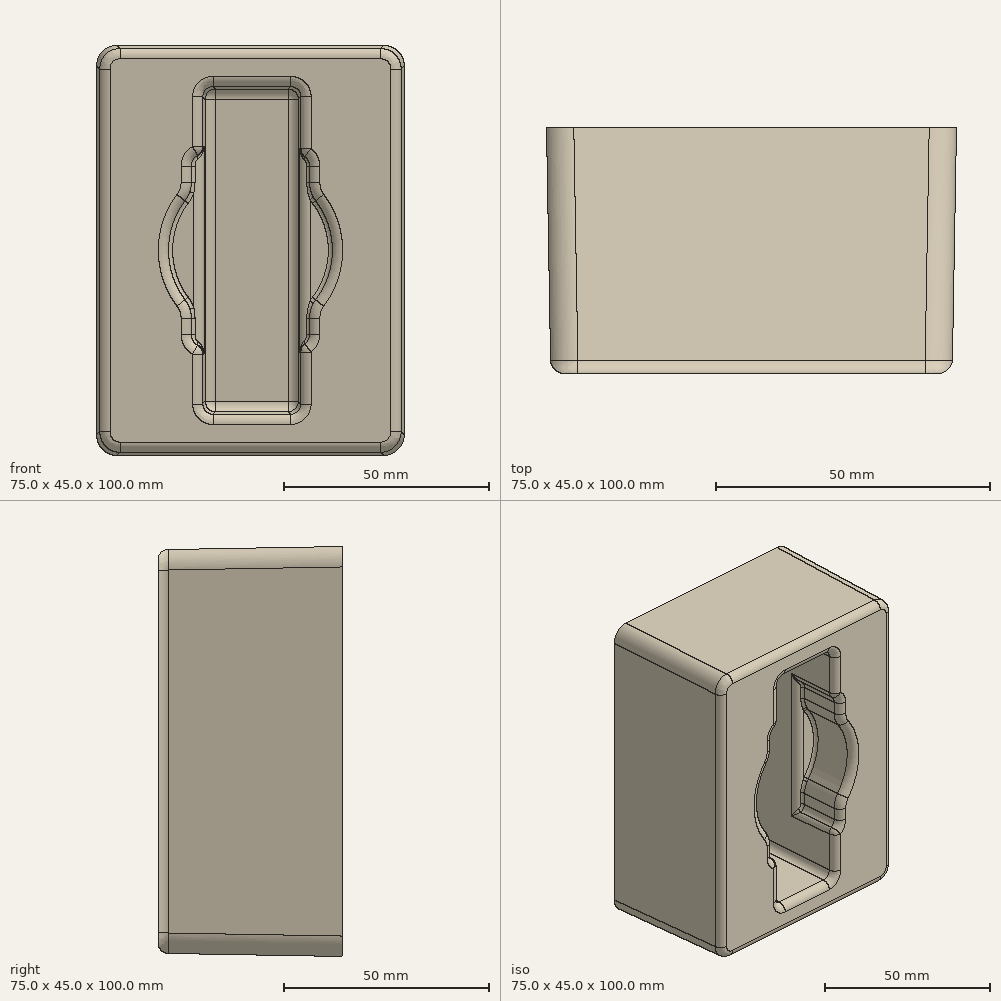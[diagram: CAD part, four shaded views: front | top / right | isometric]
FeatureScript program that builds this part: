
annotation { "Feature Type Name" : "Feature", "Feature Type Description" : "" }
export const myFeature = defineFeature(function(context is Context, id is Id, definition is map)
    precondition{}
    {
        {
            var Q0;
            Q0=qCreatedBy(makeId("Front.planeOp"),FACE);
            var sketch = newSketch(context, id + "F0", { "sketchPlane" : qUnion([Q0])});
            skLineSegment(sketch, "E0.bottom", {"start": v(0, 0) * mm, "end": v(75, 0) * mm});
            skLineSegment(sketch, "E0.top", {"start": v(0, 100) * mm, "end": v(75, 100) * mm});
            skLineSegment(sketch, "E0.left", {"start": v(0, 0) * mm, "end": v(0, 100) * mm});
            skLineSegment(sketch, "E0.right", {"start": v(75, 0) * mm, "end": v(75, 100) * mm});
            skSolve(sketch);
        }
        {
            var Q0;
            Q0=makeQuery(id+"F0.imprint","IMPRINT",FACE,{"disambiguationData":[TD([[makeQuery(id+"F0.imprint","IMPRINT",EDGE,{"derivedFrom":sQuery(id+"F0.wireOp",EDGE,"E0.bottom")}),1.0]])]});
            extrude(context, id + "F1", {"entities" : qUnion([Q0]), "depth" : 45 * mm, "hasDraft" : true, "draftAngle" : 1 * degree, "draftPullDirection" : true});
        }
        {
            var Q0;
            Q0=makeQuery(id+"F1.opExtrude","CAP_FACE",FACE,{"disambiguationData":[OSD([sQuery(id+"F0.wireOp",EDGE,"E0.bottom"),sQuery(id+"F0.wireOp",EDGE,"E0.top"),sQuery(id+"F0.wireOp",EDGE,"E0.left"),sQuery(id+"F0.wireOp",EDGE,"E0.right")])],"isStart":false});
            var sketch = newSketch(context, id + "F2", { "sketchPlane" : qUnion([Q0])});
            skArc(sketch, "E1", {"start": v(21.57, 62.1) * mm, "mid": v(17.5, 50) * mm, "end": v(21.57, 37.9) * mm});
            skLineSegment(sketch, "E2.bottom", {"start": v(48.9, 26.5) * mm, "end": v(26.1, 26.5) * mm});
            skLineSegment(sketch, "E2.top", {"start": v(48.9, 73.5) * mm, "end": v(26.1, 73.5) * mm});
            skLineSegment(sketch, "E2.left", {"start": v(51.9, 29.5) * mm, "end": v(51.9, 33.37) * mm});
            skLineSegment(sketch, "E2.right", {"start": v(23.1, 29.5) * mm, "end": v(23.1, 33.37) * mm});
            skLineSegment(sketch, "E3.trimOffspring", {"start": v(23.1, 66.63) * mm, "end": v(23.1, 70.5) * mm});
            skArc(sketch, "E4.trimOffspring", {"start": v(53.43, 37.9) * mm, "mid": v(57.5, 50) * mm, "end": v(53.43, 62.1) * mm});
            skLineSegment(sketch, "E5.trimOffspring", {"start": v(51.9, 66.63) * mm, "end": v(51.9, 70.5) * mm});
            skPoint(sketch, "E6.visualSharp", {"position": v(23.1, 63.88) * mm});
            skArc(sketch, "E6.filletArc", {"start": v(21.57, 62.1) * mm, "mid": v(22.7, 64.24) * mm, "end": v(23.1, 66.63) * mm});
            skPoint(sketch, "E7.visualSharp", {"position": v(51.9, 63.88) * mm});
            skArc(sketch, "E7.filletArc", {"start": v(51.9, 66.63) * mm, "mid": v(52.3, 64.24) * mm, "end": v(53.43, 62.1) * mm});
            skPoint(sketch, "E8.visualSharp", {"position": v(23.1, 36.12) * mm});
            skArc(sketch, "E8.filletArc", {"start": v(23.1, 33.37) * mm, "mid": v(22.7, 35.76) * mm, "end": v(21.57, 37.9) * mm});
            skPoint(sketch, "E9.visualSharp", {"position": v(51.9, 36.12) * mm});
            skArc(sketch, "E9.filletArc", {"start": v(53.43, 37.9) * mm, "mid": v(52.3, 35.76) * mm, "end": v(51.9, 33.37) * mm});
            skPoint(sketch, "E10.visualSharp", {"position": v(23.1, 73.5) * mm});
            skArc(sketch, "E10.filletArc", {"start": v(26.1, 73.5) * mm, "mid": v(23.97, 72.62) * mm, "end": v(23.1, 70.5) * mm});
            skPoint(sketch, "E11.visualSharp", {"position": v(51.9, 73.5) * mm});
            skArc(sketch, "E11.filletArc", {"start": v(51.9, 70.5) * mm, "mid": v(51.03, 72.62) * mm, "end": v(48.9, 73.5) * mm});
            skPoint(sketch, "E12.visualSharp", {"position": v(23.1, 26.5) * mm});
            skArc(sketch, "E12.filletArc", {"start": v(23.1, 29.5) * mm, "mid": v(23.97, 27.38) * mm, "end": v(26.1, 26.5) * mm});
            skPoint(sketch, "E13.visualSharp", {"position": v(51.9, 26.5) * mm});
            skArc(sketch, "E13.filletArc", {"start": v(48.9, 26.5) * mm, "mid": v(51.03, 27.38) * mm, "end": v(51.9, 29.5) * mm});
            skSolve(sketch);
        }
        {
            var Q0;
            Q0=makeQuery(id+"F2.imprint","IMPRINT",FACE,{"disambiguationData":[TD([[makeQuery(id+"F2.imprint","IMPRINT",EDGE,{"derivedFrom":sQuery(id+"F2.wireOp",EDGE,"E1")}),-1.0]])]});
            var sketch = newSketch(context, id + "F3", { "sketchPlane" : qUnion([Q0])});
            skLineSegment(sketch, "E14.bottom", {"start": v(49.85, 10) * mm, "end": v(25.85, 10) * mm});
            skLineSegment(sketch, "E14.top", {"start": v(49.85, 90) * mm, "end": v(25.85, 90) * mm});
            skLineSegment(sketch, "E14.left", {"start": v(49.85, 10) * mm, "end": v(49.85, 90) * mm});
            skLineSegment(sketch, "E14.right", {"start": v(25.85, 10) * mm, "end": v(25.85, 90) * mm});
            skPoint(sketch, "E14.middle", {"position": v(37.85, 50) * mm});
            skSolve(sketch);
        }
        {
            var Q0;
            Q0 = qSketchRegion(id + "F3", true);
            extrude(context, id + "F4", {"entities" : qUnion([Q0]), "operationType" : NewBodyOperationType.REMOVE, "oppositeDirection" : true, "depth" : 40 * mm, "hasDraft" : true, "draftAngle" : 1 * degree, "draftPullDirection" : true});
        }
        {
            var Q0;
            Q0 = qSketchRegion(id + "F2", true);
            extrude(context, id + "F5", {"entities" : qUnion([Q0]), "operationType" : NewBodyOperationType.REMOVE, "oppositeDirection" : true, "depth" : 16 * mm});
        }
        {
            var Q0;
            Q0=makeQuery(id+"F1.opExtrude","CAP_FACE",FACE,{"disambiguationData":[OSD([sQuery(id+"F0.wireOp",EDGE,"E0.bottom"),sQuery(id+"F0.wireOp",EDGE,"E0.top"),sQuery(id+"F0.wireOp",EDGE,"E0.left"),sQuery(id+"F0.wireOp",EDGE,"E0.right")])],"isStart":false});
            var Q1;
            Q1=makeQuery(id+"F4.boolean.opBoolean","COPY",EDGE,{"derivedFrom":makeQuery(id+"F4.opExtrude","SWEPT_EDGE",EDGE,{"disambiguationData":[OSD([sQuery(id+"F3.wireOp",EDGE,"E14.top"),sQuery(id+"F3.wireOp",EDGE,"E14.right")])]})});
            var Q2;
            Q2=makeQuery(id+"F4.boolean.opBoolean","COPY",EDGE,{"derivedFrom":makeQuery(id+"F4.opExtrude","SWEPT_EDGE",EDGE,{"disambiguationData":[OSD([sQuery(id+"F3.wireOp",EDGE,"E14.top"),sQuery(id+"F3.wireOp",EDGE,"E14.left")])]})});
            var Q3;
            Q3=makeQuery(id+"F4.boolean.opBoolean","COPY",FACE,{"derivedFrom":makeQuery(id+"F4.opExtrude","SWEPT_FACE",FACE,{"disambiguationData":[OSD([sQuery(id+"F3.wireOp",EDGE,"E14.bottom")])]})});
            var Q4;
            Q4=makeQuery(id+"F4.boolean.opBoolean","COPY",FACE,{"derivedFrom":makeQuery(id+"F4.opExtrude","CAP_FACE",FACE,{"disambiguationData":[OSD([sQuery(id+"F3.wireOp",EDGE,"E14.bottom"),sQuery(id+"F3.wireOp",EDGE,"E14.top"),sQuery(id+"F3.wireOp",EDGE,"E14.left"),sQuery(id+"F3.wireOp",EDGE,"E14.right")])],"isStart":false})});
            var Q5;
            Q5=makeQuery(id+"F5.boolean.opBoolean","INTERSECT",EDGE,{"derivedFrom":[makeQuery(id+"F4.boolean.opBoolean","COPY",FACE,{"derivedFrom":makeQuery(id+"F4.opExtrude","SWEPT_FACE",FACE,{"disambiguationData":[OSD([sQuery(id+"F3.wireOp",EDGE,"E14.right")])]})}),makeQuery(id+"F5.opExtrude","SWEPT_FACE",FACE,{"disambiguationData":[OSD([sQuery(id+"F2.wireOp",EDGE,"E10.filletArc")])]})]});
            var Q6;
            Q6=makeQuery(id+"F5.boolean.opBoolean","INTERSECT",EDGE,{"derivedFrom":[makeQuery(id+"F4.boolean.opBoolean","COPY",FACE,{"derivedFrom":makeQuery(id+"F4.opExtrude","SWEPT_FACE",FACE,{"disambiguationData":[OSD([sQuery(id+"F3.wireOp",EDGE,"E14.right")])]})}),makeQuery(id+"F5.opExtrude","CAP_FACE",FACE,{"disambiguationData":[OSD([sQuery(id+"F2.wireOp",EDGE,"E1"),sQuery(id+"F2.wireOp",EDGE,"E2.bottom"),sQuery(id+"F2.wireOp",EDGE,"E2.top"),sQuery(id+"F2.wireOp",EDGE,"E2.left"),sQuery(id+"F2.wireOp",EDGE,"E2.right"),sQuery(id+"F2.wireOp",EDGE,"E3.trimOffspring"),sQuery(id+"F2.wireOp",EDGE,"E4.trimOffspring"),sQuery(id+"F2.wireOp",EDGE,"E5.trimOffspring"),sQuery(id+"F2.wireOp",EDGE,"E6.filletArc"),sQuery(id+"F2.wireOp",EDGE,"E7.filletArc"),sQuery(id+"F2.wireOp",EDGE,"E8.filletArc"),sQuery(id+"F2.wireOp",EDGE,"E9.filletArc"),sQuery(id+"F2.wireOp",EDGE,"E10.filletArc"),sQuery(id+"F2.wireOp",EDGE,"E11.filletArc"),sQuery(id+"F2.wireOp",EDGE,"E12.filletArc"),sQuery(id+"F2.wireOp",EDGE,"E13.filletArc")])],"isStart":false})]});
            var Q7;
            Q7=makeQuery(id+"F5.boolean.opBoolean","INTERSECT",EDGE,{"derivedFrom":[makeQuery(id+"F4.boolean.opBoolean","COPY",FACE,{"derivedFrom":makeQuery(id+"F4.opExtrude","SWEPT_FACE",FACE,{"disambiguationData":[OSD([sQuery(id+"F3.wireOp",EDGE,"E14.right")])]})}),makeQuery(id+"F5.opExtrude","SWEPT_FACE",FACE,{"disambiguationData":[OSD([sQuery(id+"F2.wireOp",EDGE,"E12.filletArc")])]})]});
            var Q8;
            Q8=makeQuery(id+"F5.boolean.opBoolean","INTERSECT",EDGE,{"derivedFrom":[makeQuery(id+"F4.boolean.opBoolean","COPY",FACE,{"derivedFrom":makeQuery(id+"F4.opExtrude","SWEPT_FACE",FACE,{"disambiguationData":[OSD([sQuery(id+"F3.wireOp",EDGE,"E14.left")])]})}),makeQuery(id+"F5.opExtrude","SWEPT_FACE",FACE,{"disambiguationData":[OSD([sQuery(id+"F2.wireOp",EDGE,"E11.filletArc")])]})]});
            var Q9;
            Q9=makeQuery(id+"F5.boolean.opBoolean","INTERSECT",EDGE,{"derivedFrom":[makeQuery(id+"F4.boolean.opBoolean","COPY",FACE,{"derivedFrom":makeQuery(id+"F4.opExtrude","SWEPT_FACE",FACE,{"disambiguationData":[OSD([sQuery(id+"F3.wireOp",EDGE,"E14.left")])]})}),makeQuery(id+"F5.opExtrude","CAP_FACE",FACE,{"disambiguationData":[OSD([sQuery(id+"F2.wireOp",EDGE,"E1"),sQuery(id+"F2.wireOp",EDGE,"E2.bottom"),sQuery(id+"F2.wireOp",EDGE,"E2.top"),sQuery(id+"F2.wireOp",EDGE,"E2.left"),sQuery(id+"F2.wireOp",EDGE,"E2.right"),sQuery(id+"F2.wireOp",EDGE,"E3.trimOffspring"),sQuery(id+"F2.wireOp",EDGE,"E4.trimOffspring"),sQuery(id+"F2.wireOp",EDGE,"E5.trimOffspring"),sQuery(id+"F2.wireOp",EDGE,"E6.filletArc"),sQuery(id+"F2.wireOp",EDGE,"E7.filletArc"),sQuery(id+"F2.wireOp",EDGE,"E8.filletArc"),sQuery(id+"F2.wireOp",EDGE,"E9.filletArc"),sQuery(id+"F2.wireOp",EDGE,"E10.filletArc"),sQuery(id+"F2.wireOp",EDGE,"E11.filletArc"),sQuery(id+"F2.wireOp",EDGE,"E12.filletArc"),sQuery(id+"F2.wireOp",EDGE,"E13.filletArc")])],"isStart":false})]});
            var Q10;
            Q10=makeQuery(id+"F5.boolean.opBoolean","INTERSECT",EDGE,{"derivedFrom":[makeQuery(id+"F4.boolean.opBoolean","COPY",FACE,{"derivedFrom":makeQuery(id+"F4.opExtrude","SWEPT_FACE",FACE,{"disambiguationData":[OSD([sQuery(id+"F3.wireOp",EDGE,"E14.left")])]})}),makeQuery(id+"F5.opExtrude","SWEPT_FACE",FACE,{"disambiguationData":[OSD([sQuery(id+"F2.wireOp",EDGE,"E13.filletArc")])]})]});
            fillet(context, id + "F6", {"entities" : qUnion([Q0, Q1, Q2, Q3, Q4, Q5, Q6, Q7, Q8, Q9, Q10]), "radius" : 2.5 * mm, "tangentPropagation" : true, "allowEdgeOverflow" : false});
        }
        {
            var Q0;
            Q0=makeQuery(id+"F1.opExtrude","SWEPT_EDGE",EDGE,{"disambiguationData":[OSD([sQuery(id+"F0.wireOp",EDGE,"E0.bottom"),sQuery(id+"F0.wireOp",EDGE,"E0.right")])]});
            var Q1;
            Q1=makeQuery(id+"F1.opExtrude","SWEPT_EDGE",EDGE,{"disambiguationData":[OSD([sQuery(id+"F0.wireOp",EDGE,"E0.top"),sQuery(id+"F0.wireOp",EDGE,"E0.right")])]});
            var Q2;
            Q2=makeQuery(id+"F1.opExtrude","SWEPT_EDGE",EDGE,{"disambiguationData":[OSD([sQuery(id+"F0.wireOp",EDGE,"E0.top"),sQuery(id+"F0.wireOp",EDGE,"E0.left")])]});
            var Q3;
            Q3=makeQuery(id+"F1.opExtrude","SWEPT_EDGE",EDGE,{"disambiguationData":[OSD([sQuery(id+"F0.wireOp",EDGE,"E0.bottom"),sQuery(id+"F0.wireOp",EDGE,"E0.left")])]});
            fillet(context, id + "F7", {"entities" : qUnion([Q0, Q1, Q2, Q3]), "radius" : 5 * mm, "tangentPropagation" : true, "allowEdgeOverflow" : false});
        }
        {
            var Q0;
            {var subQ0=sQuery(id+"F2.wireOp",EDGE,"E2.top");var subQ1=sQuery(id+"F2.wireOp",EDGE,"E1");var subQ2=sQuery(id+"F2.wireOp",EDGE,"E2.bottom");var subQ3=sQuery(id+"F2.wireOp",EDGE,"E10.filletArc");var subQ4=sQuery(id+"F2.wireOp",EDGE,"E2.right");var subQ5=sQuery(id+"F2.wireOp",EDGE,"E3.trimOffspring");var subQ6=sQuery(id+"F2.wireOp",EDGE,"E6.filletArc");var subQ7=sQuery(id+"F2.wireOp",EDGE,"E8.filletArc");var subQ8=sQuery(id+"F2.wireOp",EDGE,"E12.filletArc");Q0=makeQuery(id+"F5.boolean.opBoolean","COPY",FACE,{"disambiguationData":[TD([makeQuery(id+"F4.boolean.opBoolean","COPY",FACE,{"derivedFrom":makeQuery(id+"F4.opExtrude","SWEPT_FACE",FACE,{"disambiguationData":[OSD([sQuery(id+"F3.wireOp",EDGE,"E14.right")])]})})])],"derivedFrom":makeQuery(id+"F5.opExtrude","CAP_FACE",FACE,{"disambiguationData":[OSD([subQ1,subQ2,subQ0,sQuery(id+"F2.wireOp",EDGE,"E2.left"),subQ4,subQ5,sQuery(id+"F2.wireOp",EDGE,"E4.trimOffspring"),sQuery(id+"F2.wireOp",EDGE,"E5.trimOffspring"),subQ6,sQuery(id+"F2.wireOp",EDGE,"E7.filletArc"),subQ7,sQuery(id+"F2.wireOp",EDGE,"E9.filletArc"),subQ3,sQuery(id+"F2.wireOp",EDGE,"E11.filletArc"),subQ8,sQuery(id+"F2.wireOp",EDGE,"E13.filletArc")])],"isStart":false})});}
            fillet(context, id + "F8", {"entities" : qUnion([Q0]), "radius" : 1 * mm, "tangentPropagation" : true, "allowEdgeOverflow" : false});
        }
        {
            var Q0;
            {var subQ0=sQuery(id+"F2.wireOp",EDGE,"E5.trimOffspring");var subQ1=sQuery(id+"F2.wireOp",EDGE,"E4.trimOffspring");var subQ2=sQuery(id+"F2.wireOp",EDGE,"E2.left");var subQ3=sQuery(id+"F2.wireOp",EDGE,"E7.filletArc");var subQ4=sQuery(id+"F2.wireOp",EDGE,"E9.filletArc");var subQ5=sQuery(id+"F2.wireOp",EDGE,"E11.filletArc");var subQ6=sQuery(id+"F2.wireOp",EDGE,"E13.filletArc");Q0=makeQuery(id+"F5.boolean.opBoolean","COPY",FACE,{"disambiguationData":[TD([makeQuery(id+"F4.boolean.opBoolean","COPY",FACE,{"derivedFrom":makeQuery(id+"F4.opExtrude","SWEPT_FACE",FACE,{"disambiguationData":[OSD([sQuery(id+"F3.wireOp",EDGE,"E14.left")])]})})])],"derivedFrom":makeQuery(id+"F5.opExtrude","CAP_FACE",FACE,{"disambiguationData":[OSD([sQuery(id+"F2.wireOp",EDGE,"E1"),sQuery(id+"F2.wireOp",EDGE,"E2.bottom"),sQuery(id+"F2.wireOp",EDGE,"E2.top"),subQ2,sQuery(id+"F2.wireOp",EDGE,"E2.right"),sQuery(id+"F2.wireOp",EDGE,"E3.trimOffspring"),subQ1,subQ0,sQuery(id+"F2.wireOp",EDGE,"E6.filletArc"),subQ3,sQuery(id+"F2.wireOp",EDGE,"E8.filletArc"),subQ4,sQuery(id+"F2.wireOp",EDGE,"E10.filletArc"),subQ5,sQuery(id+"F2.wireOp",EDGE,"E12.filletArc"),subQ6])],"isStart":false})});}
            fillet(context, id + "F9", {"entities" : qUnion([Q0]), "radius" : 1 * mm, "tangentPropagation" : true, "allowEdgeOverflow" : false});
        }
        {
            var Q0;
            Q0=makeQuery(id+"F1.opExtrude","CAP_FACE",FACE,{"disambiguationData":[OSD([sQuery(id+"F0.wireOp",EDGE,"E0.bottom"),sQuery(id+"F0.wireOp",EDGE,"E0.top"),sQuery(id+"F0.wireOp",EDGE,"E0.left"),sQuery(id+"F0.wireOp",EDGE,"E0.right")])],"isStart":true});
            shell(context, id + "F10", {"entities" : qUnion([Q0]), "thickness" : .3 * mm});
        }
    });
